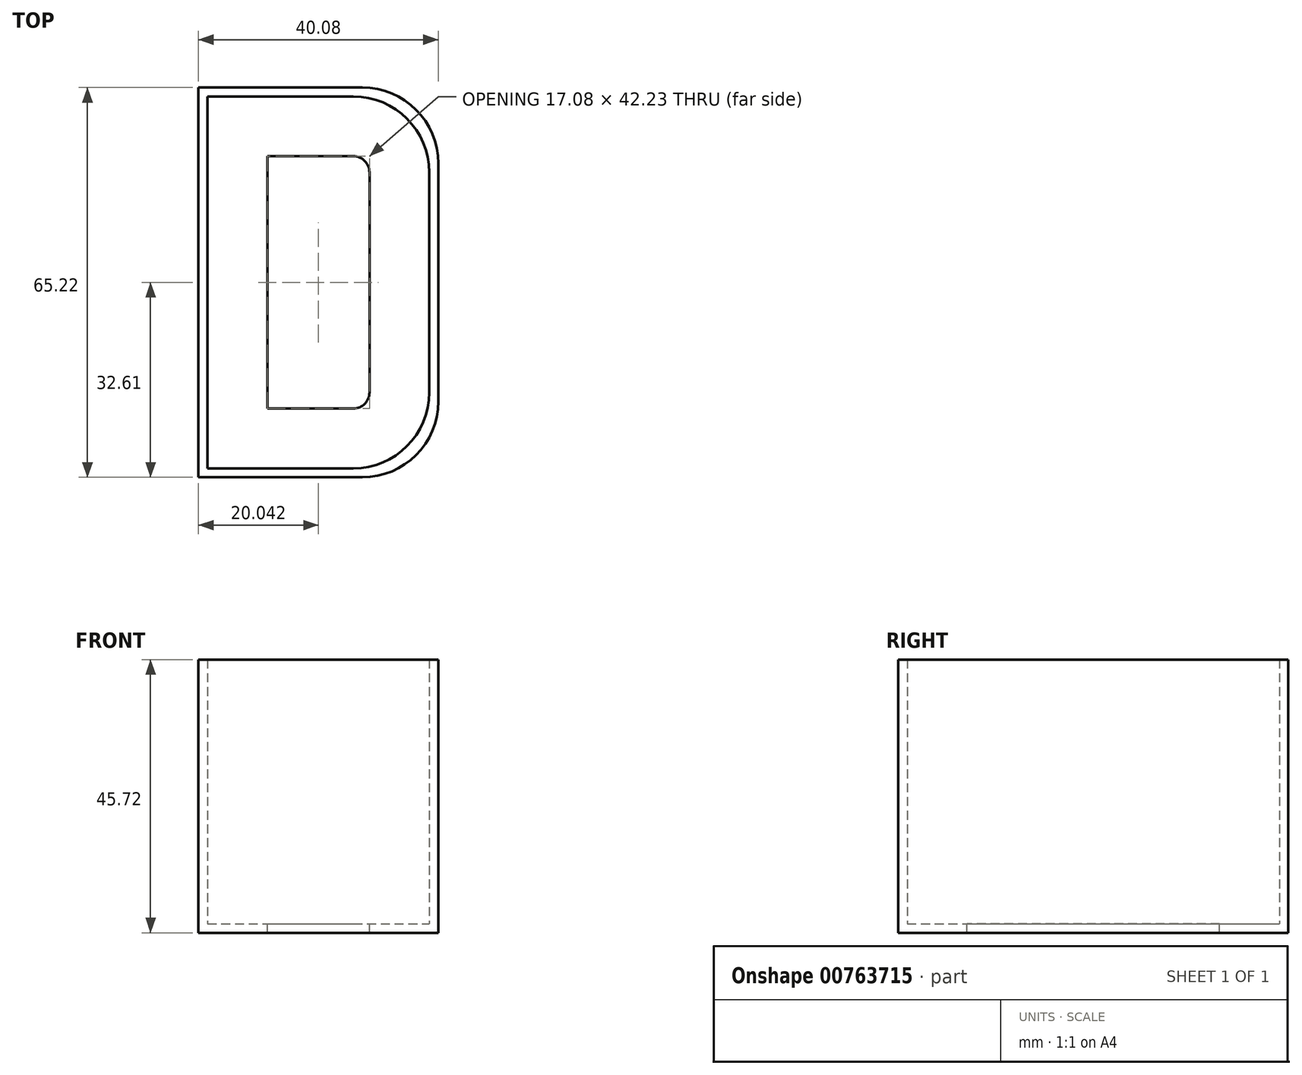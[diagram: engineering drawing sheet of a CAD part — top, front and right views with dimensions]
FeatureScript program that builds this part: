
annotation { "Feature Type Name" : "Feature", "Feature Type Description" : "" }
export const myFeature = defineFeature(function(context is Context, id is Id, definition is map)
    precondition{}
    {
        {
            var Q0;
            Q0=qCreatedBy(makeId("Front.planeOp"),FACE);
            var sketch = newSketch(context, id + "F0", { "sketchPlane" : qUnion([Q0])});
            skLineSegment(sketch, "E0.bottom", {"start": v(0, 0) * mm, "end": v(40.08, 0) * mm});
            skLineSegment(sketch, "E0.top", {"start": v(0, -45.72) * mm, "end": v(40.08, -45.72) * mm});
            skLineSegment(sketch, "E0.left", {"start": v(0, 0) * mm, "end": v(0, -45.72) * mm});
            skLineSegment(sketch, "E0.right", {"start": v(40.08, 0) * mm, "end": v(40.08, -45.72) * mm});
            skSolve(sketch);
        }
        {
            var Q0;
            Q0 = qSketchRegion(id + "F0", true);
            extrude(context, id + "F1", {"entities" : qUnion([Q0]), "endBound" : BoundingType.SYMMETRIC, "depth" : 62.23 * mm + 3 * mm, "offsetDistance" : 25.4 * mm});
        }
        {
            var Q0;
            Q0=makeQuery(id+"F1.opExtrude","SWEPT_FACE",FACE,{"disambiguationData":[OSD([sQuery(id+"F0.wireOp",EDGE,"E0.bottom")])]});
            shell(context, id + "F2", {"entities" : qUnion([Q0]), "thickness" : 1.5 * mm});
        }
        {
            var Q0;
            {var subQ0=sQuery(id+"F0.wireOp",EDGE,"E0.right");Q0=makeQuery(id+"F2.opShell","OFFSET_EDGE",EDGE,{"disambiguationData":[OSD([subQ0]),TDD([makeQuery(id+"F1.opExtrude","CAP_EDGE",EDGE,{"disambiguationData":[OSD([subQ0])],"isStart":true})])]});}
            var Q1;
            {var subQ0=sQuery(id+"F0.wireOp",EDGE,"E0.right");Q1=makeQuery(id+"F2.opShell","OFFSET_EDGE",EDGE,{"disambiguationData":[OSD([subQ0]),TDD([makeQuery(id+"F1.opExtrude","CAP_EDGE",EDGE,{"disambiguationData":[OSD([subQ0])],"isStart":false})])]});}
            var Q2;
            Q2=makeQuery(id+"F1.opExtrude","CAP_EDGE",EDGE,{"disambiguationData":[OSD([sQuery(id+"F0.wireOp",EDGE,"E0.right")])],"isStart":false});
            var Q3;
            Q3=makeQuery(id+"F1.opExtrude","CAP_EDGE",EDGE,{"disambiguationData":[OSD([sQuery(id+"F0.wireOp",EDGE,"E0.right")])],"isStart":true});
            fillet(context, id + "F3", {"entities" : qUnion([Q0, Q1, Q2, Q3]), "radius" : 12.7 * mm, "tangentPropagation" : true, "allowEdgeOverflow" : false});
        }
        {
            var Q0;
            Q0=makeQuery(id+"F2.opShell","OFFSET_FACE",FACE,{"disambiguationData":[OSD([sQuery(id+"F0.wireOp",EDGE,"E0.top")])]});
            var sketch = newSketch(context, id + "F4", { "sketchPlane" : qUnion([Q0])});
            skArc(sketch, "E1.0", {"start": v(25.88, -21.12) * mm, "mid": v(27.8, -20.32) * mm, "end": v(28.58, -18.41) * mm});
            skArc(sketch, "E1.1", {"start": v(28.58, 18.41) * mm, "mid": v(27.8, 20.32) * mm, "end": v(25.88, 21.12) * mm});
            skLineSegment(sketch, "E1.2", {"start": v(25.88, 21.12) * mm, "end": v(11.5, 21.12) * mm});
            skLineSegment(sketch, "E1.3", {"start": v(28.58, -18.41) * mm, "end": v(28.58, 18.41) * mm});
            skLineSegment(sketch, "E1.4", {"start": v(11.5, 21.12) * mm, "end": v(11.5, -21.12) * mm});
            skLineSegment(sketch, "E1.5", {"start": v(11.5, -21.12) * mm, "end": v(25.88, -21.12) * mm});
            skSolve(sketch);
        }
        {
            var Q0;
            Q0 = qSketchRegion(id + "F4", true);
            extrude(context, id + "F5", {"entities" : qUnion([Q0]), "operationType" : NewBodyOperationType.REMOVE, "oppositeDirection" : true, "depth" : 25.4 * mm, "offsetDistance" : 25.4 * mm});
        }
    });
